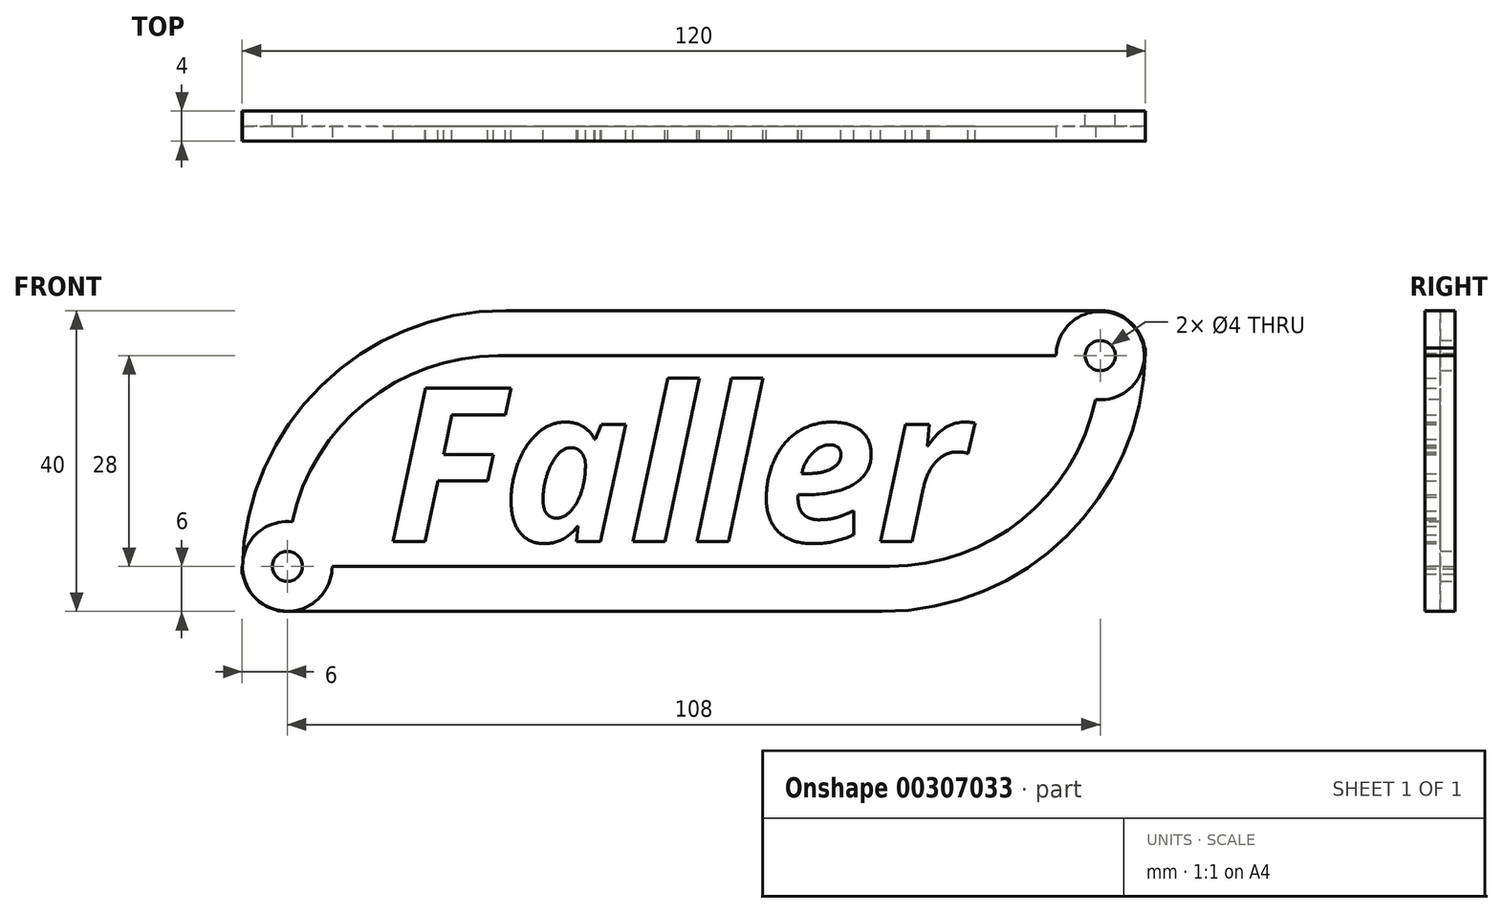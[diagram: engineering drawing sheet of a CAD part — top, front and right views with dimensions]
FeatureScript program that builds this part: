
annotation { "Feature Type Name" : "Feature", "Feature Type Description" : "" }
export const myFeature = defineFeature(function(context is Context, id is Id, definition is map)
    precondition{}
    {
        {
            var Q0;
            Q0=qCreatedBy(makeId("Front.planeOp"),FACE);
            var sketch = newSketch(context, id + "F0", { "sketchPlane" : qUnion([Q0])});
            skLineSegment(sketch, "E0.bottom", {"start": v(6, 0) * mm, "end": v(85, 0) * mm});
            skLineSegment(sketch, "E0.top", {"start": v(35, 40) * mm, "end": v(114, 40) * mm});
            skLineSegment(sketch, "E0.left", {"start": v(0, 5) * mm, "end": v(0, 6) * mm});
            skLineSegment(sketch, "E0.right", {"start": v(120, 34) * mm, "end": v(120, 35) * mm});
            skLineSegment(sketch, "E1", {"start": v(114, 0) * mm, "end": v(114, 40) * mm, "construction": true});
            skLineSegment(sketch, "E2", {"start": v(6, 0) * mm, "end": v(6, 40) * mm, "construction": true});
            skLineSegment(sketch, "E3", {"start": v(120, 6) * mm, "end": v(0, 6) * mm, "construction": true});
            skLineSegment(sketch, "E4", {"start": v(120, 34) * mm, "end": v(0, 34) * mm, "construction": true});
            skPoint(sketch, "E5.visualSharp", {"position": v(120, 40) * mm});
            skArc(sketch, "E5.filletArc", {"start": v(120, 34) * mm, "mid": v(118.24, 38.24) * mm, "end": v(114, 40) * mm});
            skPoint(sketch, "E6.visualSharp", {"position": v(0, 0) * mm});
            skArc(sketch, "E6.filletArc", {"start": v(0, 6) * mm, "mid": v(1.76, 1.76) * mm, "end": v(6, 0) * mm});
            skPoint(sketch, "E7.visualSharp", {"position": v(120, 0) * mm});
            skArc(sketch, "E7.filletArc", {"start": v(85, 0) * mm, "mid": v(109.75, 10.25) * mm, "end": v(120, 35) * mm});
            skPoint(sketch, "E8.visualSharp", {"position": v(0, 40) * mm});
            skArc(sketch, "E8.filletArc", {"start": v(35, 40) * mm, "mid": v(10.25, 29.75) * mm, "end": v(0, 5) * mm});
            skCircle(sketch, "E9", {"center": v(6, 6) * mm, "radius": 2 * mm});
            skCircle(sketch, "E10", {"center": v(114, 34) * mm, "radius": 2 * mm});
            skSolve(sketch);
        }
        {
            var Q0;
            Q0=qSketchRegion(id+"F0",true);
            extrude(context, id + "F1", {"entities" : qUnion([Q0]), "depth" : 4 * mm});
        }
        {
            var Q0;
            Q0=makeQuery(id+"F1.opExtrude","CAP_FACE",FACE,{"disambiguationData":[OSD([sQuery(id+"F0.wireOp",EDGE,"E0.bottom"),sQuery(id+"F0.wireOp",EDGE,"E0.top"),sQuery(id+"F0.wireOp",EDGE,"E5.filletArc"),sQuery(id+"F0.wireOp",EDGE,"E6.filletArc"),sQuery(id+"F0.wireOp",EDGE,"E7.filletArc"),sQuery(id+"F0.wireOp",EDGE,"E8.filletArc"),sQuery(id+"F0.wireOp",EDGE,"E9"),sQuery(id+"F0.wireOp",EDGE,"E10")])],"isStart":false});
            var sketch = newSketch(context, id + "F2", { "sketchPlane" : qUnion([Q0])});
            skCircle(sketch, "E11", {"center": v(6, 6) * mm, "radius": 5.96 * mm});
            skCircle(sketch, "E12", {"center": v(114, 34) * mm, "radius": 5.87 * mm});
            skSolve(sketch);
        }
        {
            var Q0;
            Q0=qSketchRegion(id+"F2",true);
            extrude(context, id + "F3", {"entities" : qUnion([Q0]), "operationType" : NewBodyOperationType.REMOVE, "oppositeDirection" : true, "depth" : 2 * mm});
        }
        {
            var Q0;
            Q0=makeQuery(id+"F1.opExtrude","CAP_FACE",FACE,{"disambiguationData":[OSD([sQuery(id+"F0.wireOp",EDGE,"E0.bottom"),sQuery(id+"F0.wireOp",EDGE,"E0.top"),sQuery(id+"F0.wireOp",EDGE,"E5.filletArc"),sQuery(id+"F0.wireOp",EDGE,"E6.filletArc"),sQuery(id+"F0.wireOp",EDGE,"E7.filletArc"),sQuery(id+"F0.wireOp",EDGE,"E8.filletArc"),sQuery(id+"F0.wireOp",EDGE,"E9"),sQuery(id+"F0.wireOp",EDGE,"E10")])],"isStart":false});
            var sketch = newSketch(context, id + "F4", { "sketchPlane" : qUnion([Q0])});
            skLineSegment(sketch, "E13.bottom", {"start": v(6, 6) * mm, "end": v(86, 6) * mm});
            skLineSegment(sketch, "E13.top", {"start": v(34, 34) * mm, "end": v(114, 34) * mm});
            skLineSegment(sketch, "E13.left", {"start": v(6, 6) * mm, "end": v(6, 6) * mm});
            skLineSegment(sketch, "E13.right", {"start": v(114, 34) * mm, "end": v(114, 34) * mm});
            skPoint(sketch, "E14.visualSharp", {"position": v(6, 34) * mm});
            skArc(sketch, "E14.filletArc", {"start": v(34, 34) * mm, "mid": v(14.2, 25.8) * mm, "end": v(6, 6) * mm});
            skPoint(sketch, "E15.visualSharp", {"position": v(114, 6) * mm});
            skArc(sketch, "E15.filletArc", {"start": v(86, 6) * mm, "mid": v(105.8, 14.2) * mm, "end": v(114, 34) * mm});
            skSolve(sketch);
        }
        {
            var Q0;
            {var subQ0=sQuery(id+"F4.wireOp",EDGE,"E15.filletArc");var subQ1=sQuery(id+"F4.wireOp",EDGE,"E13.bottom");var subQ2=makeQuery(id+"F4.imprint","INTERSECT",VERTEX,{"derivedFrom":[subQ1,subQ0]});Q0=makeQuery(id+"F4.imprint","IMPRINT",FACE,{"disambiguationData":[TD([[makeQuery(id+"F4.imprint","IMPRINT",EDGE,{"disambiguationData":[TD([[subQ2,1.0]])],"derivedFrom":subQ1}),1.0]])]});}
            extrude(context, id + "F5", {"entities" : qUnion([Q0]), "operationType" : NewBodyOperationType.REMOVE, "oppositeDirection" : true, "depth" : 2 * mm});
        }
        {
            var Q0;
            {var subQ0=sQuery(id+"F2.wireOp",EDGE,"E12");var subQ1=sQuery(id+"F2.wireOp",EDGE,"E11");Q0=makeQuery(id+"F5.boolean.opBoolean","MERGE",FACE,{"derivedFrom":[makeQuery(id+"F3.boolean.opBoolean","COPY",FACE,{"derivedFrom":makeQuery(id+"F3.opExtrude","CAP_FACE",FACE,{"disambiguationData":[OSD([subQ1])],"isStart":false})}),makeQuery(id+"F3.boolean.opBoolean","COPY",FACE,{"derivedFrom":makeQuery(id+"F3.opExtrude","CAP_FACE",FACE,{"disambiguationData":[OSD([subQ0])],"isStart":false})}),makeQuery(id+"F5.opExtrude","CAP_FACE",FACE,{"disambiguationData":[OSD([subQ1,subQ0,sQuery(id+"F4.wireOp",EDGE,"E13.bottom"),sQuery(id+"F4.wireOp",EDGE,"E13.top"),sQuery(id+"F4.wireOp",EDGE,"E14.filletArc"),sQuery(id+"F4.wireOp",EDGE,"E15.filletArc")])],"isStart":false})]});}
            var sketch = newSketch(context, id + "F6", { "sketchPlane" : qUnion([Q0])});
            skText(sketch, "E16", { "text": "Faller", "fontName": "OpenSans-BoldItalic.ttf"});
            const initialGuessF6  = {"E16": [0.01932, 0.0093, 1, 0, 0.02055]};
            skSetInitialGuess(sketch, initialGuessF6);
            skSolve(sketch);
        }
        {
            var Q0;
            Q0=qSketchRegion(id+"F6",true);
            extrude(context, id + "F7", {"entities" : qUnion([Q0]), "operationType" : NewBodyOperationType.ADD, "depth" : 2 * mm});
        }
    });
